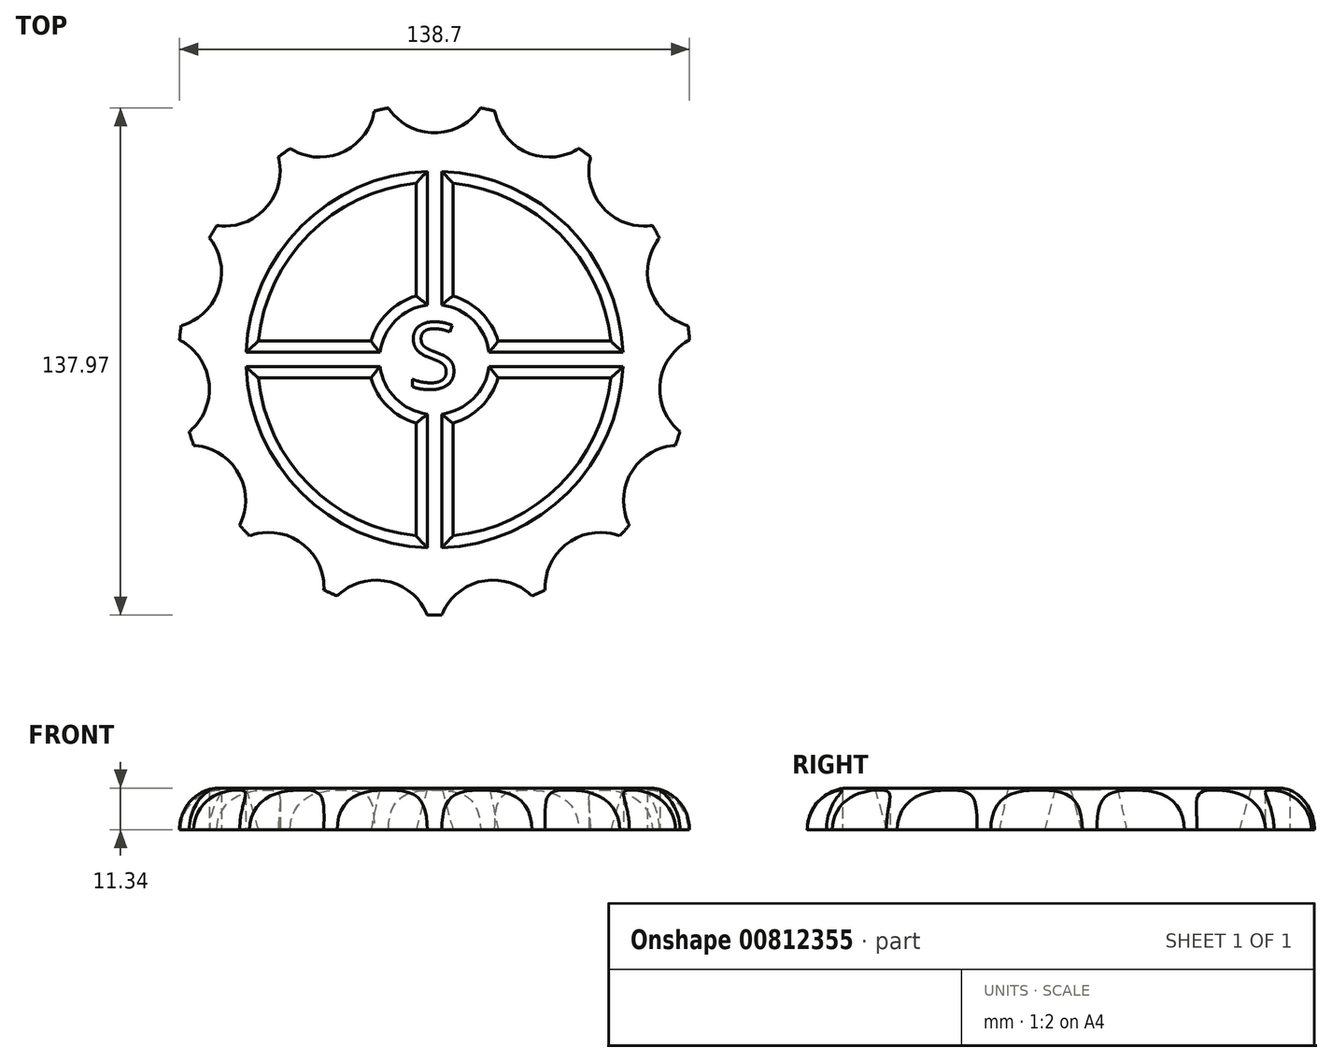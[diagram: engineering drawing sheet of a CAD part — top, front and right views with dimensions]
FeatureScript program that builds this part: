
annotation { "Feature Type Name" : "Feature", "Feature Type Description" : "" }
export const myFeature = defineFeature(function(context is Context, id is Id, definition is map)
    precondition{}
    {
        {
            var Q0;
            Q0=qCreatedBy(makeId("Front.planeOp"),FACE);
            var sketch = newSketch(context, id + "F0", { "sketchPlane" : qUnion([Q0])});
            skArc(sketch, "E0", {"start": v(-58.21, 11.34) * mm, "mid": v(-66.23, 8.02) * mm, "end": v(-69.55, 0) * mm});
            skLineSegment(sketch, "E1", {"start": v(-58.21, 11.34) * mm, "end": v(0, 11.34) * mm});
            skLineSegment(sketch, "E2", {"start": v(0, 0) * mm, "end": v(-69.55, 0) * mm});
            skLineSegment(sketch, "E3", {"start": v(0, 0) * mm, "end": v(0, 11.34) * mm});
            skSolve(sketch);
        }
        {
            var Q0;
            Q0=makeQuery(id+"F0.imprint","IMPRINT",FACE,{"disambiguationData":[TD([[makeQuery(id+"F0.imprint","IMPRINT",EDGE,{"derivedFrom":sQuery(id+"F0.wireOp",EDGE,"E0")}),1.0]])]});
            var Q1;
            Q1=sQuery(id+"F0.wireOp",EDGE,"E3");
            revolve(context, id + "F1", {"surfaceOperationType" : NewSurfaceOperationType.NEW, "entities" : qUnion([Q0]), "axis" : qUnion([Q1]), "revolveType" : RevolveType.FULL});
        }
        {
            var Q0;
            Q0=qCreatedBy(makeId("Top.planeOp"),FACE);
            var sketch = newSketch(context, id + "F2", { "sketchPlane" : qUnion([Q0])});
            skArc(sketch, "E4.cCircle", {"start": v(-56.36, -49.48) * mm, "mid": v(-55.74, -50.18) * mm, "end": v(-55.1, -50.88) * mm});
            skLineSegment(sketch, "E4.9", {"start": v(-31.19, 70.05) * mm, "end": v(-16.51, 73.17) * mm});
            skLineSegment(sketch, "E4.11", {"start": v(43.32, 61.23) * mm, "end": v(44.85, 60.12) * mm});
            skLineSegment(sketch, "E4.12", {"start": v(64.48, 38.32) * mm, "end": v(65.42, 36.68) * mm});
            skPoint(sketch, "E4.0.midPoint", {"position": v(55.74, -50.18) * mm});
            skCircle(sketch, "E5", {"center": v(0, 76.68) * mm, "radius": 15 * mm});
            skCircle(sketch, "E6", {"center": v(-31.19, 70.05) * mm, "radius": 15 * mm});
            skCircle(sketch, "E7", {"center": v(-56.98, 51.3) * mm, "radius": 15 * mm});
            skCircle(sketch, "E8", {"center": v(-72.92, 23.7) * mm, "radius": 15 * mm});
            skCircle(sketch, "E9", {"center": v(-76.26, -8.01) * mm, "radius": 15 * mm});
            skCircle(sketch, "E10", {"center": v(-66.4, -38.34) * mm, "radius": 15 * mm});
            skCircle(sketch, "E11", {"center": v(-45.07, -62.03) * mm, "radius": 15 * mm});
            skCircle(sketch, "E12", {"center": v(-15.94, -75) * mm, "radius": 15 * mm});
            skCircle(sketch, "E13", {"center": v(15.94, -75) * mm, "radius": 15 * mm});
            skCircle(sketch, "E14", {"center": v(45.07, -62.03) * mm, "radius": 15 * mm});
            skCircle(sketch, "E15", {"center": v(66.4, -38.34) * mm, "radius": 15 * mm});
            skCircle(sketch, "E16", {"center": v(76.26, -8.01) * mm, "radius": 15 * mm});
            skCircle(sketch, "E17", {"center": v(72.92, 23.7) * mm, "radius": 15 * mm});
            skCircle(sketch, "E18", {"center": v(56.98, 51.3) * mm, "radius": 15 * mm});
            skCircle(sketch, "E19", {"center": v(31.19, 70.05) * mm, "radius": 15 * mm});
            skLineSegment(sketch, "E20", {"start": v(0, 0) * mm, "end": v(0, 76.68) * mm});
            skArc(sketch, "E21.trimOffspring", {"start": v(-31.36, -68.13) * mm, "mid": v(-30.5, -68.52) * mm, "end": v(-29.64, -68.9) * mm});
            skArc(sketch, "E22.trimOffspring", {"start": v(65.42, 36.68) * mm, "mid": v(64.95, 37.5) * mm, "end": v(64.48, 38.31) * mm});
            skArc(sketch, "E23.trimOffspring", {"start": v(44.84, 60.12) * mm, "mid": v(44.08, 60.68) * mm, "end": v(43.32, 61.23) * mm});
            skSolve(sketch);
        }
        {
            var Q0;
            Q0 = qSketchRegion(id + "F2", true);
            extrude(context, id + "F3", {"entities" : qUnion([Q0]), "operationType" : NewBodyOperationType.REMOVE, "oppositeDirection" : true, "depth" : -25 * mm, "offsetDistance" : 25 * mm});
        }
        {
            var Q0;
            Q0=makeQuery(id+"F1.opRevolve","SWEPT_FACE",FACE,{"disambiguationData":[OSD([sQuery(id+"F0.wireOp",EDGE,"E2")])]});
            var sketch = newSketch(context, id + "F4", { "sketchPlane" : qUnion([Q0])});
            skCircle(sketch, "E24.0", {"center": v(0, 0) * mm, "radius": 48.21 * mm});
            skLineSegment(sketch, "E25.0", {"start": v(-17.3, 5) * mm, "end": v(-47.95, 5) * mm});
            skLineSegment(sketch, "E26.0", {"start": v(-5, 47.95) * mm, "end": v(-5, 17.3) * mm});
            skLineSegment(sketch, "E27.0", {"start": v(5, 47.95) * mm, "end": v(5, 17.3) * mm});
            skLineSegment(sketch, "E28.0", {"start": v(17.3, -5) * mm, "end": v(47.95, -5) * mm});
            skLineSegment(sketch, "E29.0", {"start": v(17.3, 5) * mm, "end": v(47.95, 5) * mm});
            skLineSegment(sketch, "E30.0", {"start": v(-17.3, -5) * mm, "end": v(-47.95, -5) * mm});
            skLineSegment(sketch, "E31.trimOffspring", {"start": v(-5, -17.3) * mm, "end": v(-5, -47.95) * mm});
            skLineSegment(sketch, "E32.trimOffspring", {"start": v(5, -17.3) * mm, "end": v(5, -47.95) * mm});
            skPoint(sketch, "E33.start.orphan", {"position": v(-2.4, 59.19) * mm});
            skCircle(sketch, "E34", {"center": v(0, 0) * mm, "radius": 18 * mm});
            skSolve(sketch);
        }
        {
            var Q0;
            {var subQ0=sQuery(id+"F4.wireOp",EDGE,"E25.0");Q0=makeQuery(id+"F4.imprint","IMPRINT",FACE,{"disambiguationData":[TD([[makeQuery(id+"F4.imprint","IMPRINT",EDGE,{"derivedFrom":subQ0}),-1.0]])]});}
            var Q1;
            {var subQ0=sQuery(id+"F4.wireOp",EDGE,"E27.0");Q1=makeQuery(id+"F4.imprint","IMPRINT",FACE,{"disambiguationData":[TD([[makeQuery(id+"F4.imprint","IMPRINT",EDGE,{"derivedFrom":subQ0}),1.0]])]});}
            var Q2;
            {var subQ0=sQuery(id+"F4.wireOp",EDGE,"E28.0");Q2=makeQuery(id+"F4.imprint","IMPRINT",FACE,{"disambiguationData":[TD([[makeQuery(id+"F4.imprint","IMPRINT",EDGE,{"derivedFrom":subQ0}),-1.0]])]});}
            var Q3;
            {var subQ0=sQuery(id+"F4.wireOp",EDGE,"E30.0");Q3=makeQuery(id+"F4.imprint","IMPRINT",FACE,{"disambiguationData":[TD([[makeQuery(id+"F4.imprint","IMPRINT",EDGE,{"derivedFrom":subQ0}),1.0]])]});}
            extrude(context, id + "F5", {"entities" : qUnion([Q0, Q1, Q2, Q3]), "operationType" : NewBodyOperationType.REMOVE, "oppositeDirection" : true, "depth" : 25 * mm, "offsetDistance" : 25 * mm, "hasDraft" : true, "draftAngle" : 15 * degree});
        }
        {
            var Q0;
            Q0=makeQuery(id+"F1.opRevolve","SWEPT_FACE",FACE,{"disambiguationData":[OSD([sQuery(id+"F0.wireOp",EDGE,"E1")])]});
            var sketch = newSketch(context, id + "F6", { "sketchPlane" : qUnion([Q0])});
            skText(sketch, "E35", { "text": "S\n", "fontName": "OpenSans-Regular.ttf"});
            const initialGuessF6  = {"E35": [-0.00732, -0.00794, 1, 0, 0.0181]};
            skSetInitialGuess(sketch, initialGuessF6);
            skSolve(sketch);
        }
        {
            var Q0;
            Q0=makeQuery(id+"F6.imprint","IMPRINT",FACE,{"disambiguationData":[TD([[makeQuery(id+"F6.imprint","IMPRINT",EDGE,{"derivedFrom":sQuery(id+"F6.wireOp",EDGE,"E35.sketch_text.stroke-0")}),-1.0]])]});
            extrude(context, id + "F7", {"entities" : qUnion([Q0]), "operationType" : NewBodyOperationType.REMOVE, "oppositeDirection" : true, "depth" : .5 * mm, "offsetDistance" : 25 * mm});
        }
    });
